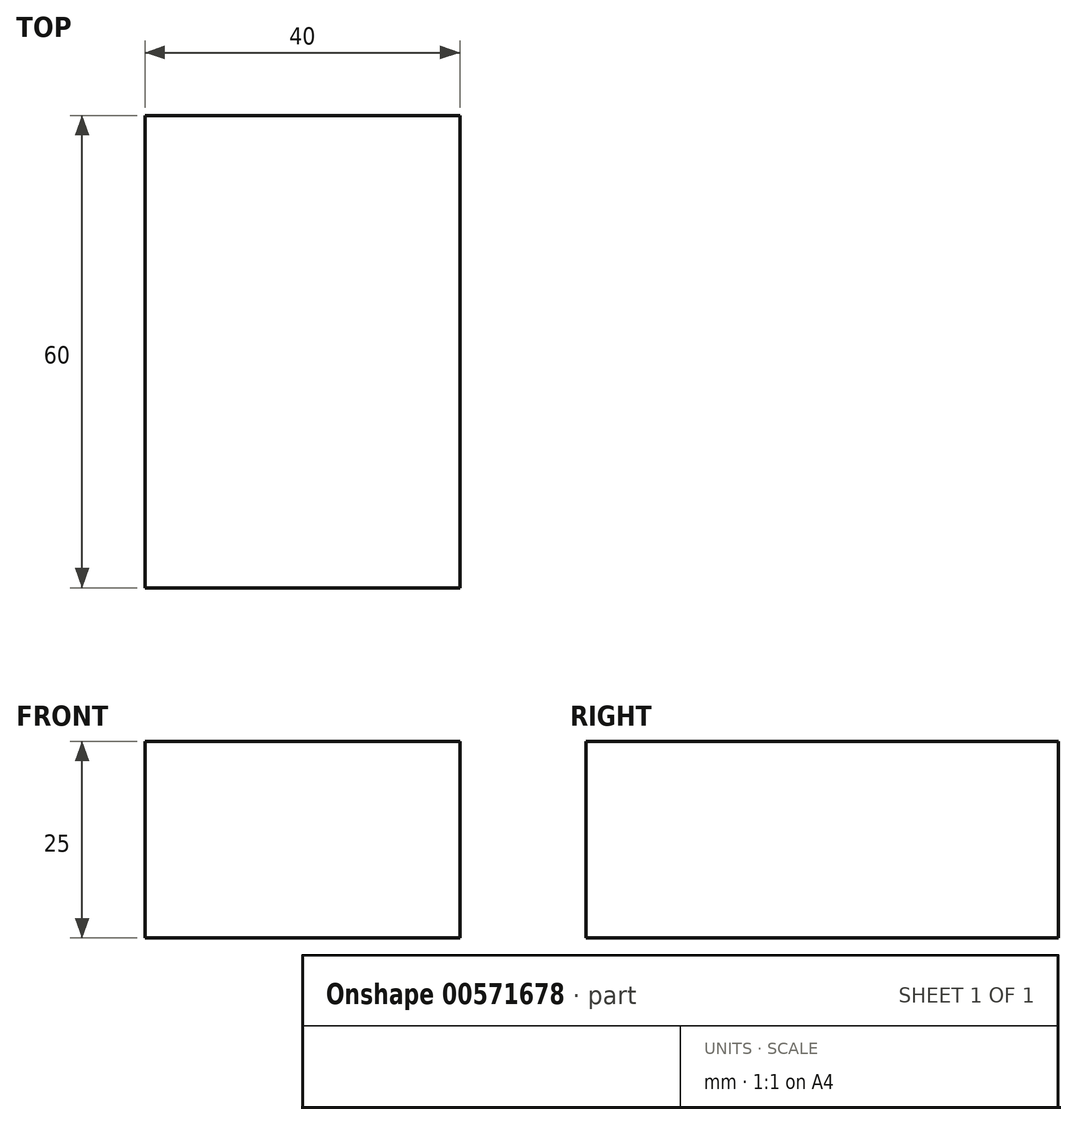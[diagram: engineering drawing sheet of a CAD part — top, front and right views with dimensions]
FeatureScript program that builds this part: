
annotation { "Feature Type Name" : "Feature", "Feature Type Description" : "" }
export const myFeature = defineFeature(function(context is Context, id is Id, definition is map)
    precondition{}
    {
        {
            var Q0;
            Q0=qCreatedBy(makeId("Top.planeOp"),FACE);
            var sketch = newSketch(context, id + "F0", { "sketchPlane" : qUnion([Q0])});
            skLineSegment(sketch, "E0.bottom", {"start": v(0, 0) * mm, "end": v(40, 0) * mm});
            skLineSegment(sketch, "E0.top", {"start": v(0, 60) * mm, "end": v(40, 60) * mm});
            skLineSegment(sketch, "E0.left", {"start": v(0, 0) * mm, "end": v(0, 60) * mm});
            skLineSegment(sketch, "E0.right", {"start": v(40, 0) * mm, "end": v(40, 60) * mm});
            skSolve(sketch);
        }
        {
            var Q0;
            Q0 = qSketchRegion(id + "F0", true);
            extrude(context, id + "F1", {"entities" : qUnion([Q0]), "depth" : 25 * mm, "offsetDistance" : 25 * mm});
        }
    });
